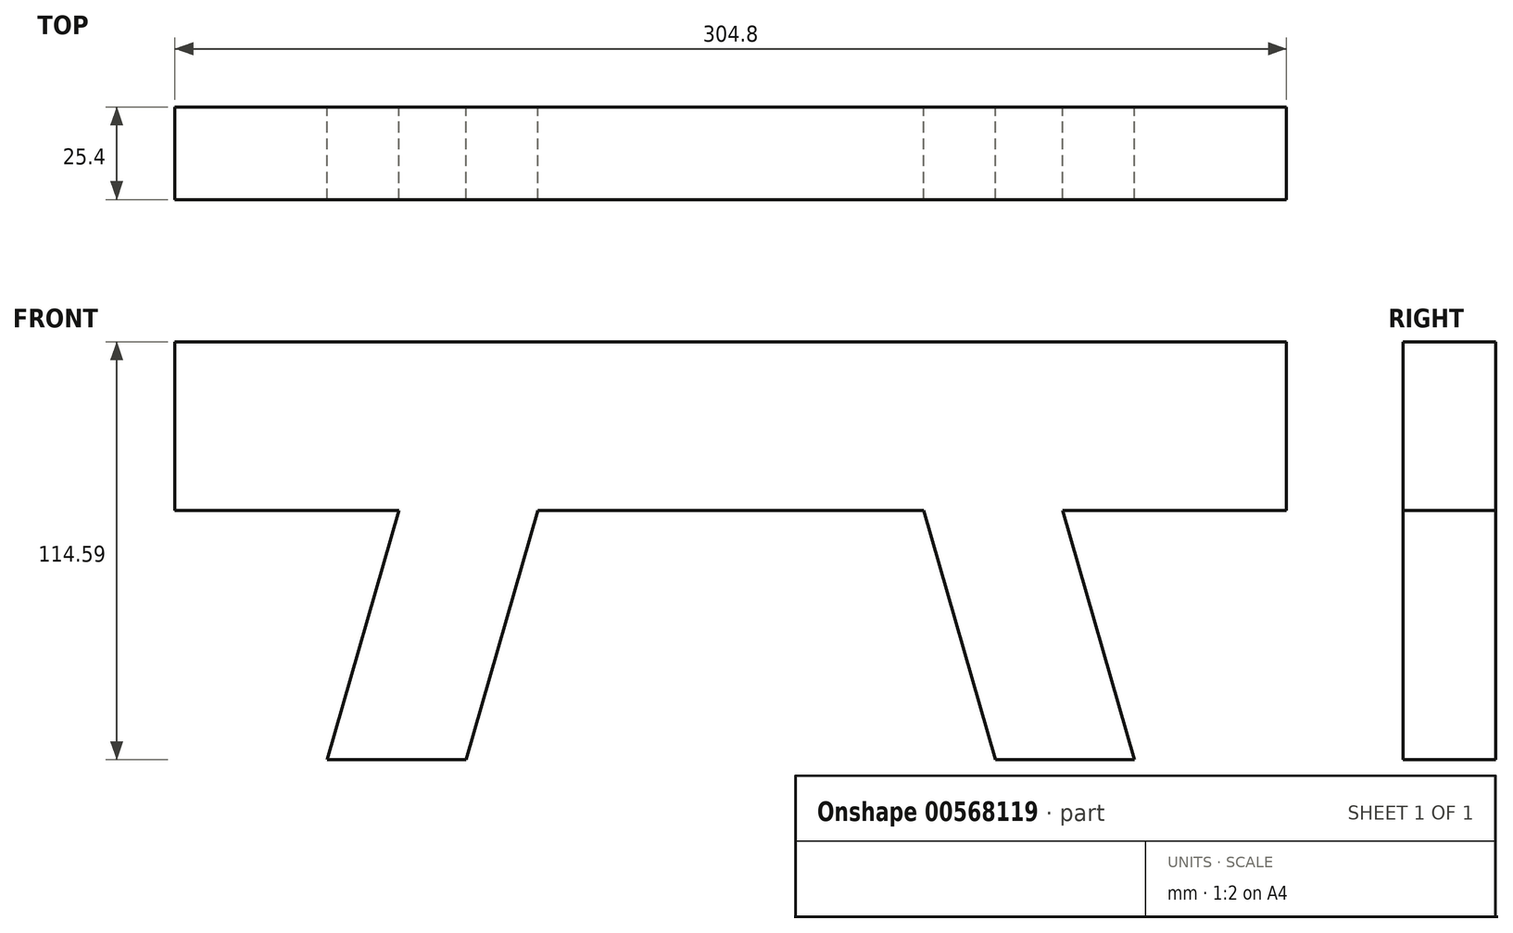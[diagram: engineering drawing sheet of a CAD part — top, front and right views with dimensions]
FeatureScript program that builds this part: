
annotation { "Feature Type Name" : "Feature", "Feature Type Description" : "" }
export const myFeature = defineFeature(function(context is Context, id is Id, definition is map)
    precondition{}
    {
        {
            var Q0;
            Q0=qCreatedBy(makeId("Front.planeOp"),FACE);
            var sketch = newSketch(context, id + "F0", { "sketchPlane" : qUnion([Q0])});
            skLineSegment(sketch, "E0.bottom", {"start": v(152.4, 23.15) * mm, "end": v(-152.4, 23.15) * mm});
            skLineSegment(sketch, "E0.top", {"start": v(152.4, -23.15) * mm, "end": v(-152.4, -23.15) * mm});
            skLineSegment(sketch, "E0.left", {"start": v(152.4, 23.15) * mm, "end": v(152.4, -23.15) * mm});
            skLineSegment(sketch, "E0.right", {"start": v(-152.4, 23.15) * mm, "end": v(-152.4, -23.15) * mm});
            skPoint(sketch, "E0.middle", {"position": v(0, 0) * mm});
            skLineSegment(sketch, "E1.bottom", {"start": v(-152.4, 23.15) * mm, "end": v(152.4, 23.15) * mm, "construction": true});
            skLineSegment(sketch, "E1.top", {"start": v(-152.4, -91.44) * mm, "end": v(152.4, -91.44) * mm, "construction": true});
            skLineSegment(sketch, "E1.left", {"start": v(-152.4, 23.15) * mm, "end": v(-152.4, -91.44) * mm, "construction": true});
            skLineSegment(sketch, "E1.right", {"start": v(152.4, 23.15) * mm, "end": v(152.4, -91.44) * mm, "construction": true});
            skLineSegment(sketch, "E2", {"start": v(90.96, -23.15) * mm, "end": v(110.63, -91.44) * mm});
            skLineSegment(sketch, "E3", {"start": v(110.63, -91.44) * mm, "end": v(72.52, -91.44) * mm});
            skLineSegment(sketch, "E4", {"start": v(72.52, -91.44) * mm, "end": v(52.86, -23.15) * mm});
            skLineSegment(sketch, "E5", {"start": v(52.86, -23.15) * mm, "end": v(90.96, -23.15) * mm});
            skLineSegment(sketch, "E6.MirrorCS", {"start": v(-152.4, -206.03) * mm, "end": v(-152.4, -91.44) * mm, "construction": true});
            skLineSegment(sketch, "E7", {"start": v(0, 0) * mm, "end": v(0, -91.44) * mm, "construction": true});
            skLineSegment(sketch, "E8.MirrorCS", {"start": v(-152.4, -23.15) * mm, "end": v(152.4, -23.15) * mm});
            skLineSegment(sketch, "E9.MirrorCS", {"start": v(-72.52, -91.44) * mm, "end": v(-52.86, -23.15) * mm});
            skLineSegment(sketch, "E10.MirrorCS", {"start": v(-110.63, -91.44) * mm, "end": v(-72.52, -91.44) * mm});
            skLineSegment(sketch, "E11.MirrorCS", {"start": v(-90.96, -23.15) * mm, "end": v(-110.63, -91.44) * mm});
            skLineSegment(sketch, "E12.MirrorCS", {"start": v(-52.86, -23.15) * mm, "end": v(-90.96, -23.15) * mm});
            skSolve(sketch);
        }
        {
            var Q0;
            Q0=makeQuery(id+"F0.imprint","IMPRINT",FACE,{"disambiguationData":[TD([[makeQuery(id+"F0.imprint","IMPRINT",EDGE,{"derivedFrom":sQuery(id+"F0.wireOp",EDGE,"E0.bottom")}),1.0]])]});
            extrude(context, id + "F1", {"entities" : qUnion([Q0]), "depth" : 25.4 * mm, "offsetDistance" : 25.4 * mm});
        }
        {
            var Q0;
            {var subQ0=sQuery(id+"F0.wireOp",EDGE,"E2");Q0=makeQuery(id+"F0.imprint","IMPRINT",FACE,{"disambiguationData":[TD([[makeQuery(id+"F0.imprint","IMPRINT",EDGE,{"derivedFrom":subQ0}),-1.0]])]});}
            var Q1;
            Q1=makeQuery(id+"F0.imprint","IMPRINT",FACE,{"disambiguationData":[TD([[makeQuery(id+"F0.imprint","IMPRINT",EDGE,{"derivedFrom":sQuery(id+"F0.wireOp",EDGE,"E9.MirrorCS")}),1.0]])]});
            extrude(context, id + "F2", {"entities" : qUnion([Q0, Q1]), "operationType" : NewBodyOperationType.ADD, "depth" : 25.4 * mm, "offsetDistance" : 25.4 * mm});
        }
    });
